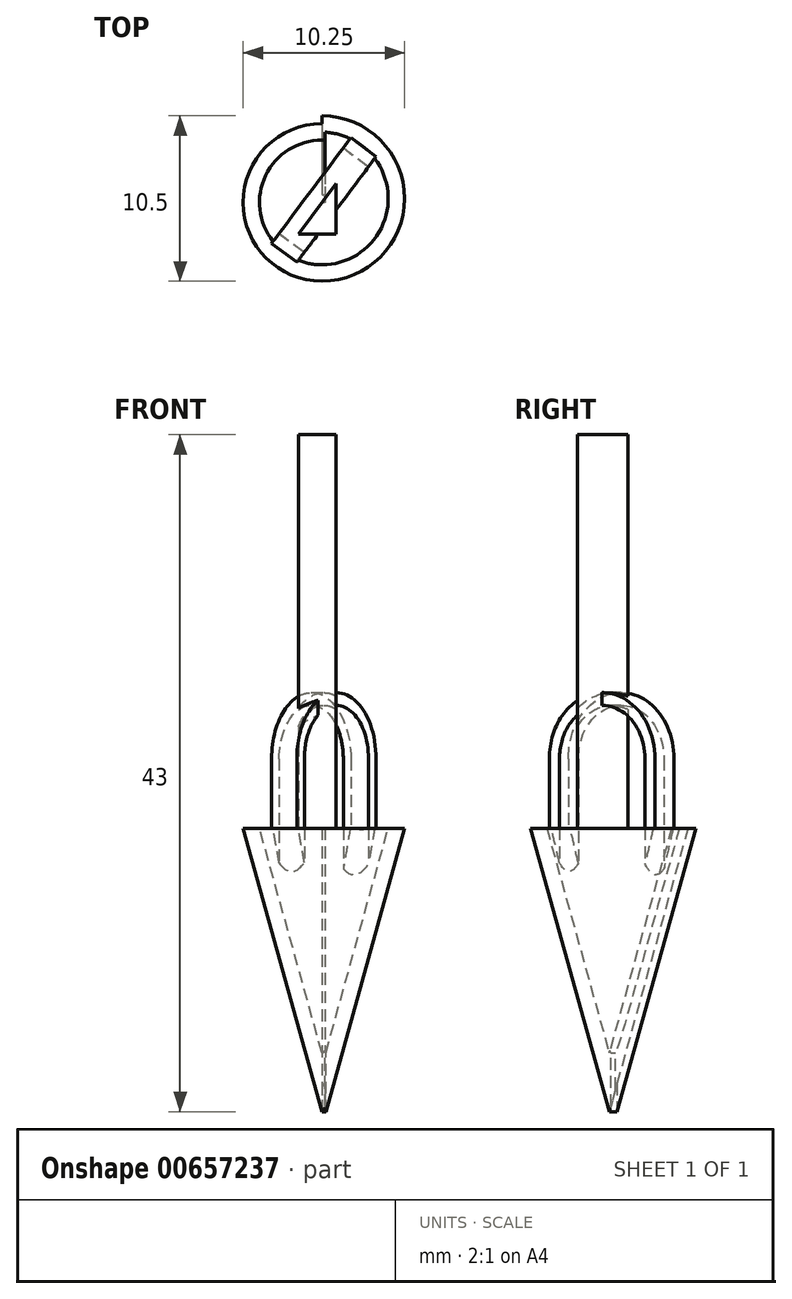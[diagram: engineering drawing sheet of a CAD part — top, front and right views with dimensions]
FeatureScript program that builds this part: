
annotation { "Feature Type Name" : "Feature", "Feature Type Description" : "" }
export const myFeature = defineFeature(function(context is Context, id is Id, definition is map)
    precondition{}
    {
        {
            var Q0;
            Q0=qCreatedBy(makeId("Top.planeOp"),FACE);
            var sketch = newSketch(context, id + "F0", { "sketchPlane" : qUnion([Q0])});
            skArc(sketch, "E0", {"start": v(0, 5) * mm, "mid": v(-5, 0) * mm, "end": v(0, -5) * mm});
            skArc(sketch, "E1", {"start": v(0, -5) * mm, "mid": v(5.25, 0.25) * mm, "end": v(0, 5.5) * mm});
            skLineSegment(sketch, "E2", {"start": v(0, 5) * mm, "end": v(0, 5.5) * mm});
            skSolve(sketch);
        }
        {
            var Q0;
            Q0=qCreatedBy(makeId("Right.planeOp"),FACE);
            var sketch = newSketch(context, id + "F1", { "sketchPlane" : qUnion([Q0])});
            skLineSegment(sketch, "E3", {"start": v(0, 0) * mm, "end": v(0, -18) * mm});
            skLineSegment(sketch, "E4", {"start": v(5, 0) * mm, "end": v(0, -18) * mm});
            skLineSegment(sketch, "E5.0", {"start": v(4.04, 0.27) * mm, "end": v(-0.96, -17.73) * mm});
            skLineSegment(sketch, "E6", {"start": v(5, 0) * mm, "end": v(3.96, 0) * mm});
            skSolve(sketch);
        }
        {
            var Q0;
            {var subQ0=sQuery(id+"F1.wireOp",EDGE,"E4");Q0=makeQuery(id+"F1.imprint","IMPRINT",FACE,{"disambiguationData":[TD([[makeQuery(id+"F1.imprint","IMPRINT",EDGE,{"derivedFrom":subQ0}),-1.0]])]});}
            var Q1;
            Q1=sQuery(id+"F0.wireOp",EDGE,"E0");
            sweep(context, id + "F2", {"profiles" : qUnion([Q0]), "path" : qUnion([Q1])});
        }
        {
            var Q0;
            Q0=makeQuery(id+"F2.opSweep","CAP_FACE",FACE,{"disambiguationData":[OSD([sQuery(id+"F0.wireOp",VERTEX,"E0.end"),sQuery(id+"F1.wireOp",EDGE,"E3"),sQuery(id+"F1.wireOp",EDGE,"E4"),sQuery(id+"F1.wireOp",EDGE,"E5.0"),sQuery(id+"F1.wireOp",EDGE,"E6")])],"isStart":false});
            var sketch = newSketch(context, id + "F3", { "sketchPlane" : qUnion([Q0])});
            skLineSegment(sketch, "E7", {"start": v(0, -14.26) * mm, "end": v(0, -18) * mm});
            skSolve(sketch);
        }
        {
            var Q0;
            Q0=makeQuery(id+"F3.imprint","IMPRINT",FACE,{"disambiguationData":[TD([[makeQuery(id+"F3.imprint","IMPRINT",EDGE,{"derivedFrom":sQuery(id+"F3.wireOp",EDGE,"E7")}),-1.0]])]});
            var Q1;
            Q1=sQuery(id+"F0.wireOp",EDGE,"E1");
            sweep(context, id + "F4", {"operationType" : NewBodyOperationType.ADD, "profiles" : qUnion([Q0]), "path" : qUnion([Q1])});
        }
        {
            var Q0;
            Q0=qCreatedBy(makeId("Top.planeOp"),FACE);
            var sketch = newSketch(context, id + "F5", { "sketchPlane" : qUnion([Q0])});
            skLineSegment(sketch, "E8.bottom", {"start": v(-1.5, 1.2) * mm, "end": v(0.91, 1.2) * mm});
            skLineSegment(sketch, "E8.top", {"start": v(-1.5, -2) * mm, "end": v(0.91, -2) * mm});
            skLineSegment(sketch, "E8.left", {"start": v(-1.5, 1.2) * mm, "end": v(-1.5, -2) * mm});
            skLineSegment(sketch, "E8.right", {"start": v(0.91, 1.2) * mm, "end": v(0.91, -2) * mm});
            skLineSegment(sketch, "E9", {"start": v(-1.5, -2) * mm, "end": v(0.91, 1.2) * mm});
            skSolve(sketch);
        }
        {
            var Q0;
            Q0=makeQuery(id+"F5.imprint","IMPRINT",FACE,{"disambiguationData":[TD([[makeQuery(id+"F5.imprint","IMPRINT",EDGE,{"derivedFrom":sQuery(id+"F5.wireOp",EDGE,"E8.top")}),1.0]])]});
            extrude(context, id + "F6", {"entities" : qUnion([Q0]), "depth" : 25 * mm, "offsetDistance" : 25 * mm});
        }
        {
            var Q0;
            Q0=makeQuery(id+"F2.opSweep","CAP_FACE",FACE,{"disambiguationData":[OSD([sQuery(id+"F0.wireOp",VERTEX,"E0.end"),sQuery(id+"F1.wireOp",EDGE,"E3"),sQuery(id+"F1.wireOp",EDGE,"E4"),sQuery(id+"F1.wireOp",EDGE,"E5.0"),sQuery(id+"F1.wireOp",EDGE,"E6")])],"isStart":false});
            extrude(context, id + "F7", {"entities" : qUnion([Q0]), "operationType" : NewBodyOperationType.ADD, "depth" : .2 * mm, "offsetDistance" : 25 * mm});
        }
        {
            var Q0;
            Q0=makeQuery(id+"F6.opExtrude","SWEPT_FACE",FACE,{"disambiguationData":[OSD([sQuery(id+"F5.wireOp",EDGE,"E9")])]});
            cPlane(context, id + "F8", {"entities" : qUnion([Q0]), "cplaneType" : CPlaneType.OFFSET, "offset" : 0 * mm, "width" : 150 * mm, "height" : 150 * mm});
        }
        {
            var Q0;
            Q0=qCreatedBy(id+"F8.planeOp",FACE);
            var sketch = newSketch(context, id + "F9", { "sketchPlane" : qUnion([Q0])});
            skArc(sketch, "E10", {"start": v(4, 4.42) * mm, "mid": v(-0.2, 8.61) * mm, "end": v(-4.4, 4.42) * mm});
            skLineSegment(sketch, "E11", {"start": v(-0.2, 4.42) * mm, "end": v(-4.4, 4.42) * mm});
            skLineSegment(sketch, "E12", {"start": v(-4.4, 4.42) * mm, "end": v(4, 4.42) * mm});
            skLineSegment(sketch, "E13", {"start": v(4, 4.42) * mm, "end": v(4, -2.86) * mm});
            skLineSegment(sketch, "E14", {"start": v(-4.4, 4.42) * mm, "end": v(-4.4, -3.24) * mm});
            skLineSegment(sketch, "E15.0", {"start": v(-3.6, 4.42) * mm, "end": v(-3.6, -3.24) * mm});
            skArc(sketch, "E15.1", {"start": v(3.2, 4.42) * mm, "mid": v(-0.2, 7.81) * mm, "end": v(-3.6, 4.42) * mm});
            skLineSegment(sketch, "E15.2", {"start": v(3.2, 4.42) * mm, "end": v(3.2, -2.86) * mm});
            skLineSegment(sketch, "E16", {"start": v(-4.4, -3.24) * mm, "end": v(-3.6, -3.24) * mm});
            skLineSegment(sketch, "E17", {"start": v(3.2, -2.86) * mm, "end": v(4, -2.86) * mm});
            skSolve(sketch);
        }
        {
            var Q0;
            {var subQ0=sQuery(id+"F9.wireOp",EDGE,"E14");Q0=makeQuery(id+"F9.imprint","IMPRINT",FACE,{"disambiguationData":[TD([[makeQuery(id+"F9.imprint","IMPRINT",EDGE,{"derivedFrom":subQ0}),1.0]])]});}
            var Q1;
            {var subQ0=sQuery(id+"F9.wireOp",EDGE,"E10");Q1=makeQuery(id+"F9.imprint","IMPRINT",FACE,{"disambiguationData":[TD([[makeQuery(id+"F9.imprint","IMPRINT",EDGE,{"derivedFrom":subQ0}),1.0]])]});}
            var Q2;
            {var subQ0=sQuery(id+"F9.wireOp",EDGE,"E13");Q2=makeQuery(id+"F9.imprint","IMPRINT",FACE,{"disambiguationData":[TD([[makeQuery(id+"F9.imprint","IMPRINT",EDGE,{"derivedFrom":subQ0}),-1.0]])]});}
            extrude(context, id + "F10", {"entities" : qUnion([Q0, Q1, Q2]), "operationType" : NewBodyOperationType.ADD, "depth" : 2 * mm, "offsetDistance" : 25 * mm, "symmetric" : true});
        }
    });
